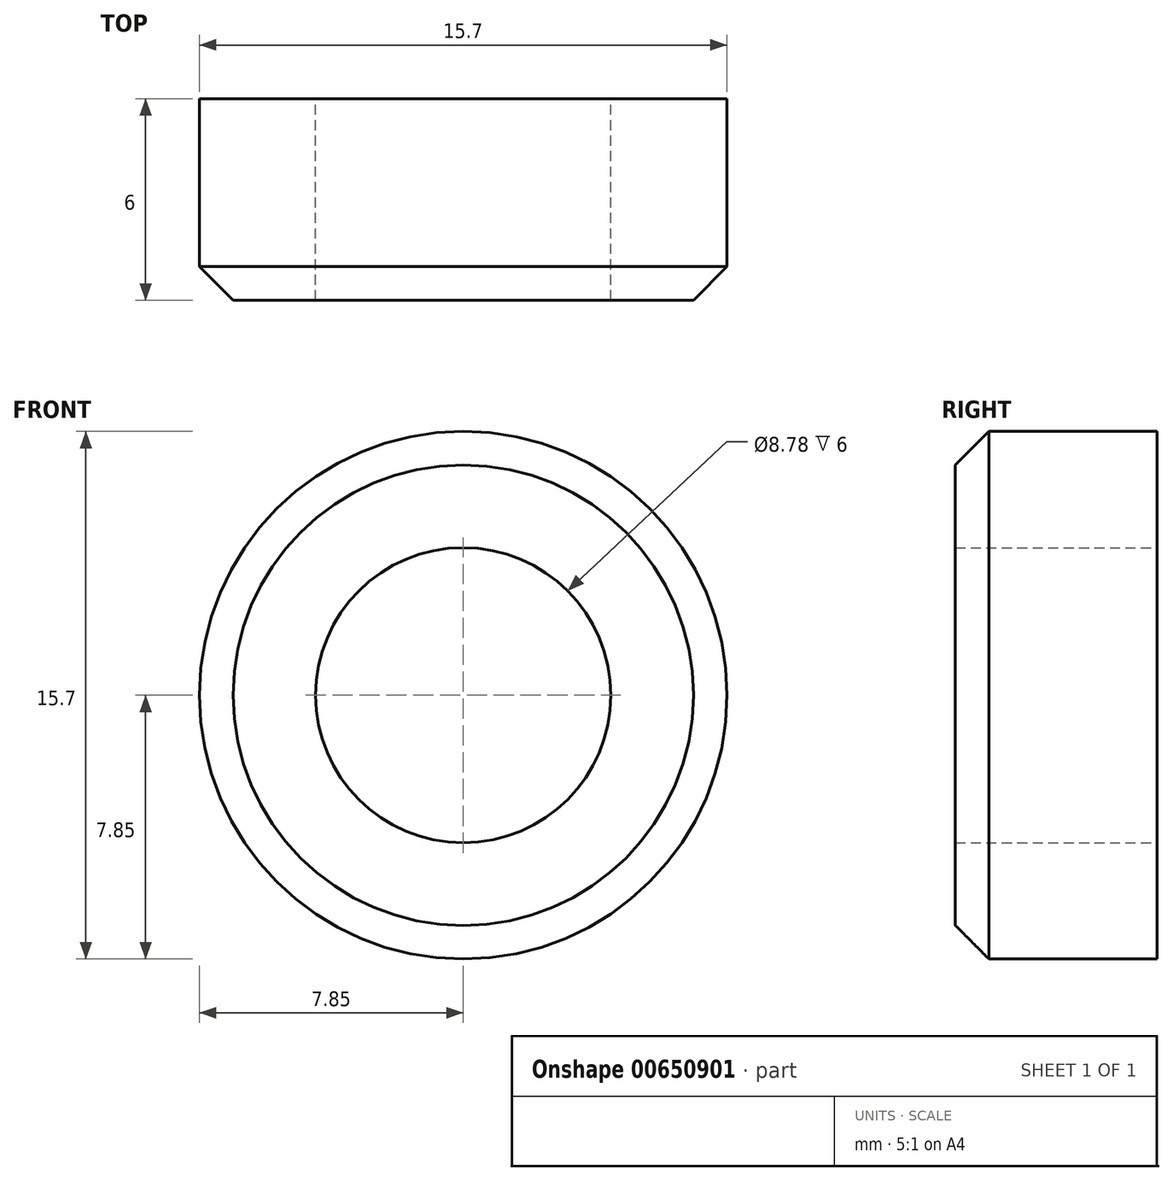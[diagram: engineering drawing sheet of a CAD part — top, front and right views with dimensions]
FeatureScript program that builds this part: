
annotation { "Feature Type Name" : "Feature", "Feature Type Description" : "" }
export const myFeature = defineFeature(function(context is Context, id is Id, definition is map)
    precondition{}
    {
        {
            var Q0;
            Q0=qCreatedBy(makeId("Front.planeOp"),FACE);
            var sketch = newSketch(context, id + "F0", { "sketchPlane" : qUnion([Q0])});
            skCircle(sketch, "E0", {"center": v(0, 0) * mm, "radius": 7.85 * mm});
            skSolve(sketch);
        }
        {
            var Q0;
            Q0=qCreatedBy(makeId("Front.planeOp"),FACE);
            var sketch = newSketch(context, id + "F1", { "sketchPlane" : qUnion([Q0])});
            skCircle(sketch, "E1", {"center": v(0, 0) * mm, "radius": 4.39 * mm});
            skSolve(sketch);
        }
        {
            var Q0;
            Q0=makeQuery(id+"F0.imprint","IMPRINT",FACE,{"disambiguationData":[TD([[makeQuery(id+"F0.imprint","IMPRINT",EDGE,{"derivedFrom":sQuery(id+"F0.wireOp",EDGE,"E0")}),1.0]])]});
            extrude(context, id + "F2", {"entities" : qUnion([Q0]), "depth" : 6 * mm, "offsetDistance" : 25 * mm});
        }
        {
            var Q0;
            Q0=sQuery(id+"F1.wireOp",VERTEX,"E1.center");
            var Q1;
            Q1=makeQuery(id+"F2.opExtrude","SWEPT_BODY",BODY,{"disambiguationData":[OSD([sQuery(id+"F0.wireOp",EDGE,"E0")])]});
            hole(context, id + "F3", {"style" : HoleStyle.SIMPLE, "endStyle" : HoleEndStyle.THROUGH, "oppositeDirection" : true, "holeDiameter" : 8.78 * mm, "majorDiameter" : 5 * mm, "isTappedThrough" : true, "tappedDepth" : 12 * mm, "tapClearance" : 3, "locations" : qUnion([Q0]), "scope" : qUnion([Q1])});
        }
        {
            var Q0;
            Q0=makeQuery(id+"F2.opExtrude","CAP_EDGE",EDGE,{"disambiguationData":[OSD([sQuery(id+"F0.wireOp",EDGE,"E0")])],"isStart":false});
            chamfer(context, id + "F4", {"entities" : qUnion([Q0]), "width" : 1 * mm, "tangentPropagation" : true});
        }
    });
